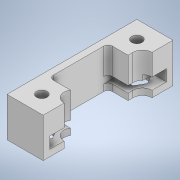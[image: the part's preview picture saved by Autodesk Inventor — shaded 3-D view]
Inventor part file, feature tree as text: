
AUTODESK INVENTOR PART (.ipt)
format: ipt  version: 2021.1 (Build 251245010, 245A)  size: 227,840 bytes
history: native  units: mm
features: extrude x5, sketch x5, other x1, fillet x1
ambient origin geometry x8: Origin, YZ Plane, XZ Plane, XY Plane, X Axis, Y Axis, Z Axis, Center Point
bodies: Body1 (feature_tree)
feature tree (12):
  other  "Твердое тело1"
  extrude  "Выдавливание1"  Depth=17.0mm
  extrude  "Выдавливание2"  Depth=17.0mm
  extrude  "Выдавливание3"  Depth=35.56mm
  fillet  "Сопряжение1"  Radius=2.0mm
  extrude  "Выдавливание4"  TaperAngle=90.0deg  [1 undecoded]
  extrude  "Выдавливание5"  Depth=0.5mm
  sketch  "Эскиз1"
  sketch  "Эскиз2"
  sketch  "Эскиз3"
  sketch  "Эскиз4"
  sketch  "Эскиз5"
note: 1 required parameter value undecoded (feature->parameter linkage not recoverable at this tier; creation-order binding heuristic only, values carry confidence <= 0.55)
